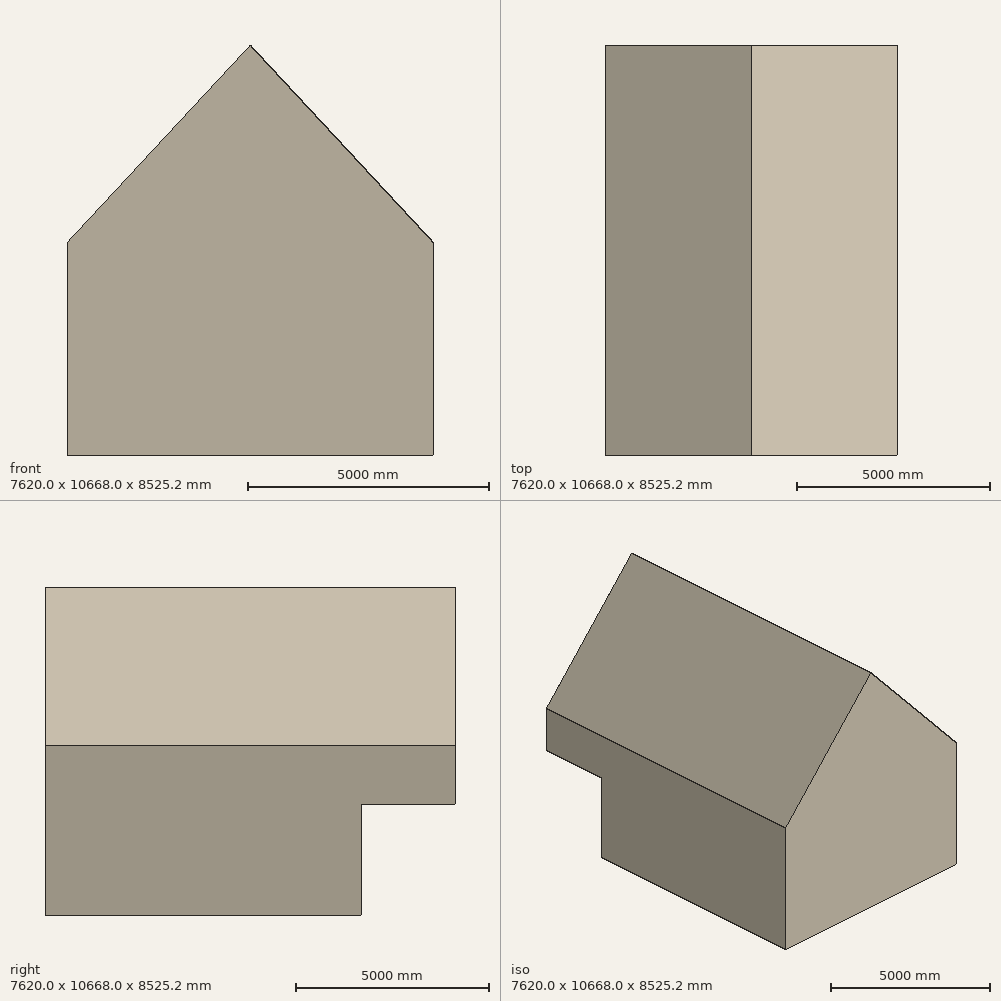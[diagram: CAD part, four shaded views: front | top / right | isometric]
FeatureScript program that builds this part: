
annotation { "Feature Type Name" : "Feature", "Feature Type Description" : "" }
export const myFeature = defineFeature(function(context is Context, id is Id, definition is map)
    precondition{}
    {
        {
            var Q0;
            Q0=qCreatedBy(makeId("Front.planeOp"),FACE);
            var sketch = newSketch(context, id + "F0", { "sketchPlane" : qUnion([Q0])});
            skLineSegment(sketch, "E0", {"start": v(0, 0) * mm, "end": v(7620, 0) * mm});
            skLineSegment(sketch, "E1", {"start": v(7620, 0) * mm, "end": v(7620, 4419.6) * mm});
            skLineSegment(sketch, "E2", {"start": v(7620, 4419.6) * mm, "end": v(0, 4419.6) * mm});
            skLineSegment(sketch, "E3", {"start": v(0, 4419.6) * mm, "end": v(0, 0) * mm});
            skLineSegment(sketch, "E4", {"start": v(7620, 4419.6) * mm, "end": v(3810, 4419.6) * mm});
            skLineSegment(sketch, "E5", {"start": v(3810, 8525.24) * mm, "end": v(0, 4419.6) * mm});
            skLineSegment(sketch, "E6", {"start": v(3810, 8525.24) * mm, "end": v(7620, 4419.6) * mm});
            skSolve(sketch);
        }
        {
            var Q0;
            Q0=makeQuery(id+"F0.imprint","IMPRINT",FACE,{"disambiguationData":[TD([[makeQuery(id+"F0.imprint","IMPRINT",EDGE,{"derivedFrom":sQuery(id+"F0.wireOp",EDGE,"E0")}),1.0]])]});
            var Q1;
            Q1=makeQuery(id+"F0.imprint","IMPRINT",FACE,{"disambiguationData":[TD([[makeQuery(id+"F0.imprint","IMPRINT",EDGE,{"derivedFrom":sQuery(id+"F0.wireOp",EDGE,"E2")}),-1.0]])]});
            extrude(context, id + "F1", {"entities" : qUnion([Q0, Q1]), "oppositeDirection" : true, "depth" : 10668 * mm});
        }
        {
            var Q0;
            Q0=makeQuery(id+"F1.opExtrude","SWEPT_FACE",FACE,{"disambiguationData":[OSD([sQuery(id+"F0.wireOp",EDGE,"E3")])]});
            var sketch = newSketch(context, id + "F2", { "sketchPlane" : qUnion([Q0])});
            skLineSegment(sketch, "E7", {"start": v(-10668, 4419.6) * mm, "end": v(-10668, 2895.6) * mm});
            skLineSegment(sketch, "E8", {"start": v(-10668, 2895.6) * mm, "end": v(-8229.6, 2895.6) * mm});
            skLineSegment(sketch, "E9", {"start": v(-8229.6, 2895.6) * mm, "end": v(-8229.6, 0) * mm});
            skLineSegment(sketch, "E10", {"start": v(-8229.6, 0) * mm, "end": v(-10668, 0) * mm});
            skLineSegment(sketch, "E11", {"start": v(-10668, 0) * mm, "end": v(-10668, 2895.6) * mm});
            skSolve(sketch);
        }
        {
            var Q0;
            Q0=makeQuery(id+"F2.imprint","IMPRINT",FACE,{"disambiguationData":[TD([[makeQuery(id+"F2.imprint","IMPRINT",EDGE,{"derivedFrom":sQuery(id+"F2.wireOp",EDGE,"E8")}),-1.0]])]});
            extrude(context, id + "F3", {"entities" : qUnion([Q0]), "operationType" : NewBodyOperationType.REMOVE, "oppositeDirection" : true, "depth" : 7620 * mm});
        }
    });
